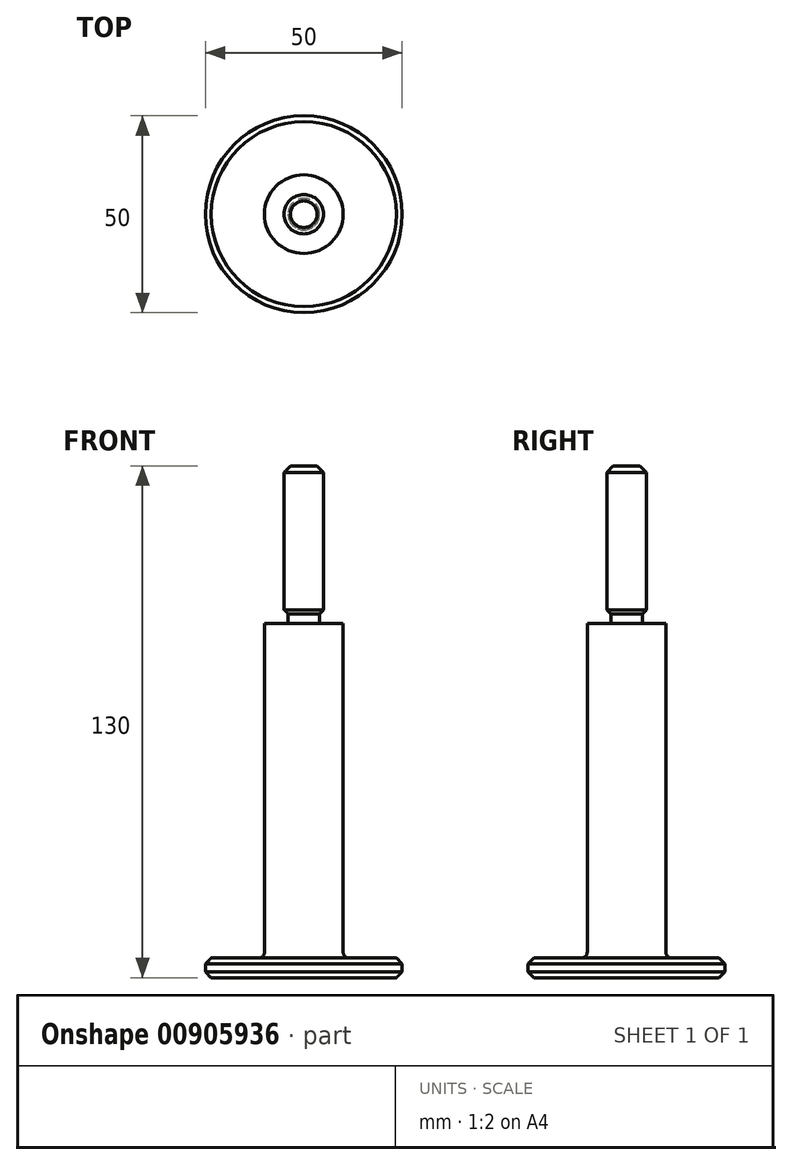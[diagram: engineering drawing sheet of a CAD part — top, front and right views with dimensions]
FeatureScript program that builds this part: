
annotation { "Feature Type Name" : "Feature", "Feature Type Description" : "" }
export const myFeature = defineFeature(function(context is Context, id is Id, definition is map)
    precondition{}
    {
        {
            var Q0;
            Q0=qCreatedBy(makeId("Front.planeOp"),FACE);
            var sketch = newSketch(context, id + "F0", { "sketchPlane" : qUnion([Q0])});
            skLineSegment(sketch, "E0", {"start": v(0, 0) * mm, "end": v(0, 130) * mm});
            skLineSegment(sketch, "E1", {"start": v(0, 130) * mm, "end": v(5, 130) * mm});
            skLineSegment(sketch, "E2", {"start": v(10, 90) * mm, "end": v(10, 5) * mm});
            skLineSegment(sketch, "E3", {"start": v(10, 5) * mm, "end": v(25, 5) * mm});
            skLineSegment(sketch, "E4", {"start": v(25, 5) * mm, "end": v(25, 0) * mm});
            skLineSegment(sketch, "E5", {"start": v(25, 0) * mm, "end": v(0, 0) * mm});
            skPoint(sketch, "E6.start.orphan", {"position": v(5, 90) * mm});
            skPoint(sketch, "E7.orphan", {"position": v(4, 90) * mm});
            skLineSegment(sketch, "E8", {"start": v(10, 90) * mm, "end": v(4, 90) * mm});
            skLineSegment(sketch, "E9", {"start": v(4, 91.85) * mm, "end": v(5, 91.85) * mm});
            skLineSegment(sketch, "E10", {"start": v(5, 130) * mm, "end": v(5, 91.85) * mm});
            skPoint(sketch, "E10.endSnap0", {"position": v(5.6, 91.85) * mm});
            skPoint(sketch, "E11.orphan", {"position": v(7.22, 91.85) * mm});
            skLineSegment(sketch, "E12", {"start": v(4, 91.85) * mm, "end": v(4, 90) * mm});
            skSolve(sketch);
        }
        {
            var Q0;
            Q0 = qSketchRegion(id + "F0", true);
            var Q1;
            Q1=sQuery(id+"F0.wireOp",EDGE,"E0");
            revolve(context, id + "F1", {"surfaceOperationType" : NewSurfaceOperationType.NEW, "entities" : qUnion([Q0]), "axis" : qUnion([Q1]), "revolveType" : RevolveType.FULL});
        }
        {
            var Q0;
            Q0=makeQuery(id+"F1.opRevolve","SWEPT_EDGE",EDGE,{"disambiguationData":[OSD([sQuery(id+"F0.wireOp",EDGE,"E2"),sQuery(id+"F0.wireOp",EDGE,"E3")])]});
            fillet(context, id + "F2", {"entities" : qUnion([Q0]), "radius" : 1.5 * mm, "tangentPropagation" : true, "allowEdgeOverflow" : false});
        }
        {
            var Q0;
            Q0=makeQuery(id+"F1.opRevolve","SWEPT_EDGE",EDGE,{"disambiguationData":[OSD([sQuery(id+"F0.wireOp",EDGE,"E3"),sQuery(id+"F0.wireOp",EDGE,"E4")])]});
            var Q1;
            Q1=makeQuery(id+"F1.opRevolve","SWEPT_EDGE",EDGE,{"disambiguationData":[OSD([sQuery(id+"F0.wireOp",EDGE,"E4"),sQuery(id+"F0.wireOp",EDGE,"E5")])]});
            chamfer(context, id + "F3", {"entities" : qUnion([Q0, Q1]), "width" : 1.5 * mm, "tangentPropagation" : true});
        }
        {
            var Q0;
            Q0=makeQuery(id+"F1.opRevolve","SWEPT_EDGE",EDGE,{"disambiguationData":[OSD([sQuery(id+"F0.wireOp",EDGE,"E1"),sQuery(id+"F0.wireOp",EDGE,"E10")])]});
            var Q1;
            Q1=makeQuery(id+"F1.opRevolve","SWEPT_EDGE",EDGE,{"disambiguationData":[OSD([sQuery(id+"F0.wireOp",EDGE,"E9"),sQuery(id+"F0.wireOp",EDGE,"E10")])]});
            chamfer(context, id + "F4", {"entities" : qUnion([Q0, Q1]), "width" : 1.6 * mm, "tangentPropagation" : true});
        }
    });
